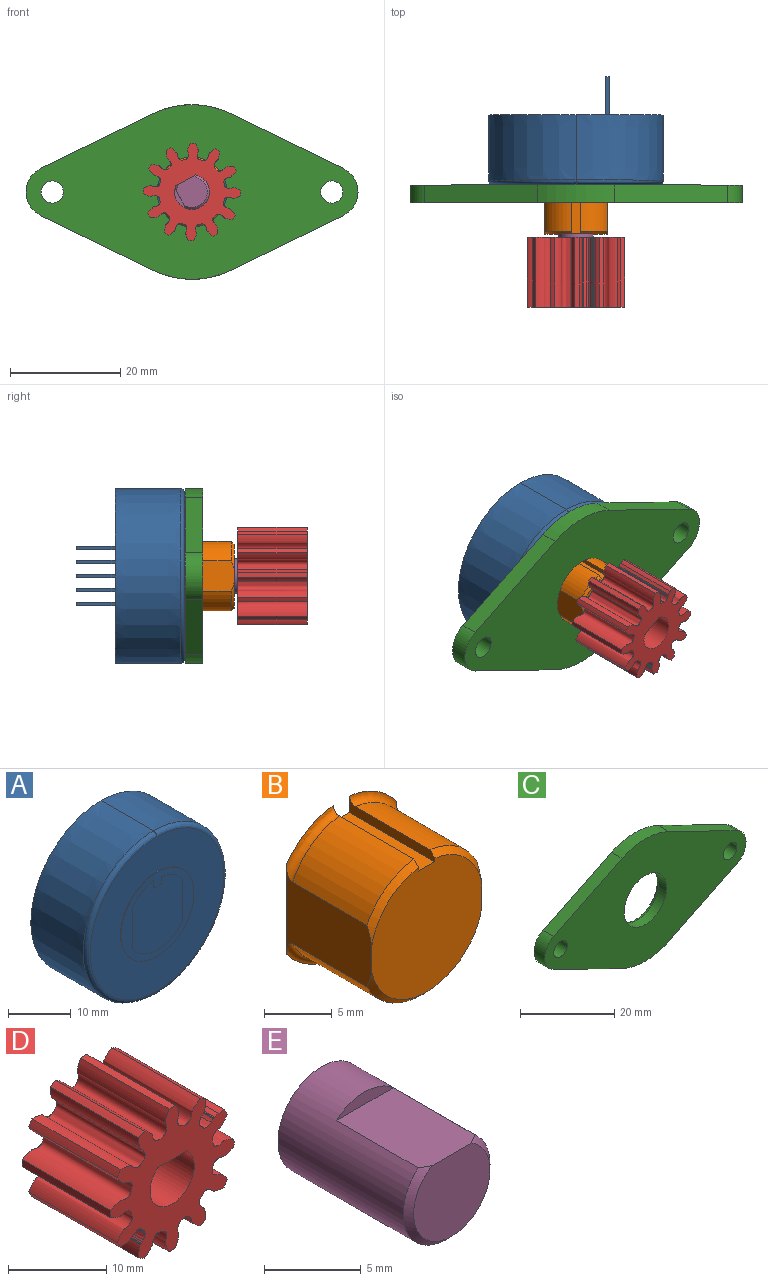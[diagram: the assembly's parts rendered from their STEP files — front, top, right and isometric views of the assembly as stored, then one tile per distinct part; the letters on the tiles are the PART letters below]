
ASSEMBLY  parts=5 mates=4
PART A: 35 faces, bbox 31.8x19.7x31.8 mm
  f0: plane 30.16x30.16mm, normal (0,-1,0), area 500mm2, adj f29,f30,f32,f33
  f1: plane 31.75x31.75mm, normal (0,1,0), area 789.7mm2, adj f2,f3,f5,f6,f7,f8,f10,f11
  f2: extruded ~31.75x15.88mm, area 589.6mm2, adj f1,f3,f32
  f3: extruded ~31.75x15.88mm, area 589.6mm2, adj f1,f2,f33
  f4: plane 0.64x0.64mm, normal (0,1,0), area 0.4mm2, adj f5,f6,f7,f8
  f5: plane 6.99x0.64mm, normal (0,0,-1), area 4.4mm2, adj f1,f4,f6,f8
  f6: plane 6.99x0.64mm, normal (1,0,0), area 4.4mm2, adj f1,f4,f5,f7
  f7: plane 6.99x0.64mm, normal (0,0,1), area 4.4mm2, adj f1,f4,f6,f8
  f8: plane 6.99x0.64mm, normal (-1,0,0), area 4.4mm2, adj f1,f4,f5,f7
  f9: plane 0.64x0.64mm, normal (0,1,0), area 0.4mm2, adj f10,f11,f12,f13
  f10: plane 6.99x0.64mm, normal (0,0,-1), area 4.4mm2, adj f1,f9,f11,f12
  f11: plane 6.99x0.64mm, normal (1,0,0), area 4.4mm2, adj f1,f9,f10,f13
  f12: plane 6.99x0.64mm, normal (-1,0,0), area 4.4mm2, adj f1,f9,f10,f13
  f13: plane 6.99x0.64mm, normal (0,0,1), area 4.4mm2, adj f1,f9,f11,f12
  f14: plane 0.64x0.64mm, normal (0,1,0), area 0.4mm2, adj f15,f16,f17,f18
  f15: plane 6.99x0.64mm, normal (-1,0,0), area 4.4mm2, adj f1,f14,f16,f17
  f16: plane 6.99x0.64mm, normal (0,0,1), area 4.4mm2, adj f1,f14,f15,f18
  f17: plane 6.99x0.64mm, normal (0,0,-1), area 4.4mm2, adj f1,f14,f15,f18
  f18: plane 6.99x0.64mm, normal (1,0,0), area 4.4mm2, adj f1,f14,f16,f17
  f19: plane 0.64x0.64mm, normal (0,1,0), area 0.4mm2, adj f20,f21,f22,f23
  f20: plane 6.99x0.64mm, normal (0,0,-1), area 4.4mm2, adj f1,f19,f21,f23
  f21: plane 6.99x0.64mm, normal (1,0,0), area 4.4mm2, adj f1,f19,f20,f22
  f22: plane 6.99x0.64mm, normal (0,0,1), area 4.4mm2, adj f1,f19,f21,f23
  f23: plane 6.99x0.64mm, normal (-1,0,0), area 4.4mm2, adj f1,f19,f20,f22
  f24: plane 0.64x0.64mm, normal (0,1,0), area 0.4mm2, adj f25,f26,f27,f28
  f25: plane 6.99x0.64mm, normal (0,0,-1), area 4.4mm2, adj f1,f24,f26,f28
  f26: plane 6.99x0.64mm, normal (1,0,0), area 4.4mm2, adj f1,f24,f25,f27
  f27: plane 6.99x0.64mm, normal (0,0,1), area 4.4mm2, adj f1,f24,f26,f28
  f28: plane 6.99x0.64mm, normal (-1,0,0), area 4.4mm2, adj f1,f24,f25,f27
  f29: extruded ~16.51x8.26mm, area 2.6mm2, adj f0,f30,f31
  f30: extruded ~16.51x8.26mm, area 2.6mm2, adj f0,f29,f31
  f31: plane 16.51x16.51mm, normal (0,-1,0), area 77.2mm2, adj f29,f30,f34
  f32: bspline ~31.75x25.88mm, area 61.3mm2, adj f0,f2,f33
  f33: bspline ~31.75x25.88mm, area 61.3mm2, adj f0,f3,f32
  f34: plane 13.92x11.43mm, normal (0,-1,0), area 136.9mm2, adj f31
PART B: 16 faces, bbox 14.5x8.9x16.1 mm
  f0: cone r=5.84mm half-angle=45deg, axis (0,1,0), area 10.7mm2, adj f3,f5,f13,f14
  f1: cone r=5.84mm half-angle=45deg, axis (0,1,0), area 4.7mm2, adj f3,f6,f12,f13
  f2: cone r=5.84mm half-angle=45deg, axis (0,1,0), area 4.7mm2, adj f3,f4,f10,f14
  f3: plane 11.62x11.43mm, normal (0,-1,0), area 106.2mm2, adj f0,f1,f2,f10,f11,f12,f13,f14
  f4: cylinder r=6.35mm len=7.75mm, axis (0,1,0), area 48.6mm2, adj f2,f9,f10,f14
  f5: cylinder r=6.35mm len=11.43mm, axis (0,1,0), area 110.2mm2, adj f0,f7,f13,f14
  f6: cylinder r=6.35mm len=7.75mm, axis (0,1,0), area 48.6mm2, adj f1,f8,f12,f13
  f7: torus R=6.99mm, axis (0,1,0), area 13.8mm2, adj f5,f13,f14,f15
  f8: torus R=6.99mm, axis (0,1,0), area 6.1mm2, adj f6,f12,f13,f15
  f9: torus R=6.99mm, axis (0,1,0), area 6.1mm2, adj f4,f10,f14,f15
  f10: plane 8.92x1.5mm, normal (-1,0,0), area 7.4mm2, adj f2,f3,f4,f9,f11,f15
  f11: plane 8.89x1.68mm, normal (0,0,1), area 14.9mm2, adj f3,f10,f12,f15
  f12: plane 8.92x1.5mm, normal (1,0,0), area 7.4mm2, adj f1,f3,f6,f8,f11,f15
  f13: plane 8.89x8.03mm, normal (-1,0,0), area 48.9mm2, adj f0,f1,f3,f5,f6,f7,f8,f15
  f14: plane 8.89x8.03mm, normal (1,0,0), area 48.9mm2, adj f0,f2,f3,f4,f5,f7,f9,f15
  f15: plane 13.92x11.43mm, normal (0,1,0), area 136.9mm2, adj f7,f8,f9,f10,f11,f12,f13,f14
PART C: 14 faces, bbox 60.3x3.2x31.8 mm
  f0: plane 20.54x9.99mm, normal (-0.44,0,-0.9), area 72.5mm2, adj f1,f7,f11,f12
  f1: cylinder r=15.88mm len=13.89mm, axis (0,1,0), area 45.6mm2, adj f0,f2,f11,f12
  f2: plane 20.54x9.99mm, normal (0.44,0,-0.9), area 72.5mm2, adj f1,f3,f11,f12
  f3: cylinder r=4.76mm len=8.57mm, axis (0,1,0), area 33.8mm2, adj f2,f4,f11,f12
  f4: plane 20.54x9.99mm, normal (0.44,0,0.9), area 72.5mm2, adj f3,f5,f11,f12
  f5: cylinder r=15.88mm len=13.89mm, axis (0,1,0), area 45.6mm2, adj f4,f6,f11,f12
  f6: plane 20.54x9.99mm, normal (-0.44,0,0.9), area 72.5mm2, adj f5,f7,f11,f12
  f7: cylinder r=4.76mm len=8.57mm, axis (0,1,0), area 33.8mm2, adj f0,f6,f11,f12
  f8: cylinder r=2.02mm len=4.04mm, axis (0,1,0), area 40.3mm2, adj f11,f12
  f9: cylinder r=2.02mm len=4.04mm, axis (0,1,0), area 40.3mm2, adj f11,f12
  f10: cylinder r=6.35mm len=12.7mm, axis (0,1,0), area 95mm2, adj f11,f13
  f11: plane 60.33x31.75mm, normal (0,-1,0), area 1069.4mm2, adj f0,f1,f2,f3,f4,f5,f6,f7
  f12: plane 60.33x31.75mm, normal (0,1,0), area 1035.7mm2, adj f0,f1,f2,f3,f4,f5,f6,f7
  f13: torus R=7.14mm, axis (0,-1,0), area 52mm2, adj f10,f12
PART D: 68 faces, bbox 18x19.2x18 mm
  f0: plane 17.95x17.95mm, normal (0,-1,0), area 143.8mm2, adj f1,f2,f3,f4,f5,f6,f7,f8
  f1: bspline ~19x1.59mm, area 19.4mm2, adj f0,f42,f53,f64
  f2: bspline ~19x0.24mm, area 1mm2, adj f0,f54,f55,f64
  f3: bspline ~19x0.35mm, area 2.9mm2, adj f0,f55,f56,f64
  f4: bspline ~19x0.28mm, area 0.9mm2, adj f0,f56,f57,f64
  f5: bspline ~19x0.24mm, area 0.6mm2, adj f0,f57,f58,f64
  f6: bspline ~19x0.2mm, area 0.4mm2, adj f0,f58,f59,f64
  f7: bspline ~19x0.5mm, area 3.2mm2, adj f0,f59,f60,f64
  f8: bspline ~19x0.49mm, area 5.4mm2, adj f0,f60,f61,f64
  f9: bspline ~19x0.28mm, area 1.3mm2, adj f0,f61,f62,f64
  f10: bspline ~19x0.95mm, area 10.1mm2, adj f0,f41,f62,f64
  f11: bspline ~19x1.59mm, area 19.4mm2, adj f0,f35,f44,f64
  f12: bspline ~19x0.24mm, area 1mm2, adj f0,f45,f46,f64
  f13: bspline ~19x0.35mm, area 2.9mm2, adj f0,f46,f47,f64
  f14: bspline ~19x0.28mm, area 0.9mm2, adj f0,f47,f48,f64
  f15: bspline ~19x0.24mm, area 0.6mm2, adj f0,f48,f49,f64
  f16: bspline ~19x0.2mm, area 0.4mm2, adj f0,f49,f50,f64
  f17: bspline ~19x0.5mm, area 3.2mm2, adj f0,f50,f51,f64
  f18: bspline ~19x0.49mm, area 5.4mm2, adj f0,f51,f52,f64
  f19: bspline ~19x0.28mm, area 1.3mm2, adj f0,f52,f63,f64
  f20: bspline ~19x0.95mm, area 10.1mm2, adj f0,f36,f63,f64
  f21: bspline ~19x3.59mm, area 91.1mm2, adj f0,f40,f42,f64
  f22: bspline ~19x3.59mm, area 91.1mm2, adj f0,f39,f40,f64
  f23: bspline ~19x3.56mm, area 91.1mm2, adj f0,f38,f39,f64
  f24: bspline ~19x3.59mm, area 91.1mm2, adj f0,f37,f38,f64
  f25: bspline ~19x3.59mm, area 91.1mm2, adj f0,f36,f37,f64
  f26: bspline ~19x3.59mm, area 91.1mm2, adj f0,f34,f35,f64
  f27: bspline ~19x3.59mm, area 91.1mm2, adj f0,f33,f34,f64
  f28: bspline ~19x3.56mm, area 91.1mm2, adj f0,f32,f33,f64
  f29: bspline ~19x3.59mm, area 91.1mm2, adj f0,f32,f43,f64
  f30: bspline ~19x3.59mm, area 91.1mm2, adj f0,f41,f43,f64
  f31: cylinder r=3.17mm len=12.7mm, axis (0,-1,0), area 195.3mm2, adj f0,f64,f67
  f32: cylinder r=8.89mm len=12.7mm, axis (0,-1,0), area 11.5mm2, adj f0,f28,f29,f64
  f33: cylinder r=8.89mm len=12.7mm, axis (0,-1,0), area 11.5mm2, adj f0,f27,f28,f64
  f34: cylinder r=8.89mm len=12.7mm, axis (0,-1,0), area 11.5mm2, adj f0,f26,f27,f64
  f35: cylinder r=8.89mm len=12.7mm, axis (0,-1,0), area 11.5mm2, adj f0,f11,f26,f64
  f36: cylinder r=8.89mm len=12.7mm, axis (0,-1,0), area 11.5mm2, adj f0,f20,f25,f64
  f37: cylinder r=8.89mm len=12.7mm, axis (0,-1,0), area 11.5mm2, adj f0,f24,f25,f64
  f38: cylinder r=8.89mm len=12.7mm, axis (0,-1,0), area 11.5mm2, adj f0,f23,f24,f64
  f39: cylinder r=8.89mm len=12.7mm, axis (0,-1,0), area 11.5mm2, adj f0,f22,f23,f64
  f40: cylinder r=8.89mm len=12.7mm, axis (0,-1,0), area 11.5mm2, adj f0,f21,f22,f64
  f41: cylinder r=8.89mm len=12.7mm, axis (0,-1,0), area 11.5mm2, adj f0,f10,f30,f64
  f42: cylinder r=8.89mm len=12.7mm, axis (0,-1,0), area 11.5mm2, adj f0,f1,f21,f64
  f43: cylinder r=8.89mm len=12.7mm, axis (0,-1,0), area 11.5mm2, adj f0,f29,f30,f64
  f44: extruded ~12.7x0.04mm, area 0.6mm2, adj f0,f11,f64,f66
  f45: extruded ~12.7x0.05mm, area 0.8mm2, adj f0,f12,f64,f66
  f46: extruded ~12.7x0.11mm, area 1.9mm2, adj f0,f12,f13,f64
  f47: extruded ~12.7x0.61mm, area 8.6mm2, adj f0,f13,f14,f64
  f48: extruded ~12.7x0.15mm, area 2mm2, adj f0,f14,f15,f64
  f49: extruded ~12.7x0.16mm, area 2.3mm2, adj f0,f15,f16,f64
  f50: extruded ~12.7x0.45mm, area 8.1mm2, adj f0,f16,f17,f64
  f51: extruded ~12.7x0.89mm, area 12.3mm2, adj f0,f17,f18,f64
  f52: extruded ~12.7x0.09mm, area 1.5mm2, adj f0,f18,f19,f64
  f53: extruded ~12.7x0.04mm, area 0.6mm2, adj f0,f1,f64,f65
  f54: extruded ~12.7x0.05mm, area 0.8mm2, adj f0,f2,f64,f65
  f55: extruded ~12.7x0.11mm, area 1.9mm2, adj f0,f2,f3,f64
  f56: extruded ~12.7x0.61mm, area 8.6mm2, adj f0,f3,f4,f64
  f57: extruded ~12.7x0.15mm, area 2mm2, adj f0,f4,f5,f64
  f58: extruded ~12.7x0.16mm, area 2.3mm2, adj f0,f5,f6,f64
  f59: extruded ~12.7x0.45mm, area 8.1mm2, adj f0,f6,f7,f64
  f60: extruded ~12.7x0.89mm, area 12.3mm2, adj f0,f7,f8,f64
  f61: extruded ~12.7x0.09mm, area 1.5mm2, adj f0,f8,f9,f64
  f62: extruded ~12.7x0.61mm, area 8.1mm2, adj f0,f9,f10,f64
  f63: extruded ~12.7x0.61mm, area 8.1mm2, adj f0,f19,f20,f64
  f64: plane 17.95x17.95mm, normal (0,1,0), area 140.7mm2, adj f1,f2,f3,f4,f5,f6,f7,f8
  f65: bspline ~19x0.27mm, area 0.1mm2, adj f53,f54,f64
  f66: bspline ~19x0.27mm, area 0.1mm2, adj f44,f45,f64
  f67: plane 12.7x4.16mm, normal (0,0,-1), area 52.8mm2, adj f0,f31,f64
PART E: 6 faces, bbox 6.3x9.5x6.3 mm
  f0: cylinder r=3.17mm len=9.14mm, axis (0,1,0), area 155mm2, adj f1,f3,f4,f5
  f1: plane 4.16x0.78mm, normal (0,-1,0), area 2.2mm2, adj f0,f3
  f2: plane 5.58x5.18mm, normal (0,-1,0), area 23.7mm2, adj f3,f5
  f3: plane 6.35x4.16mm, normal (0,0,1), area 26.2mm2, adj f0,f1,f2,f5
  f4: plane 6.34x6.34mm, normal (0,1,0), area 31.6mm2, adj f0
  f5: cone r=3.17mm half-angle=45deg, axis (0,1,0), area 8mm2, adj f0,f2,f3
PLACE A t=(-15.88,-6.17,15.88)mm
PLACE B t=(-15.88,-6.17,15.88)mm
PLACE C t=(-15.88,-6.17,15.88)mm
PLACE D rot(axis=(0,-1,0),28.7deg) t=(0,-9.55,0)mm
PLACE E rot(axis=(0,-1,0),118.7deg) t=(-6.29,-6.17,-21.55)mm
MATE fastened B.f0 <-> A.f34  axis (0,1,0) through (0,3.18,0)mm
MATE fastened C.f1 <-> A.f34  axis (0,-1,0) through (0,3.18,0)mm
MATE fastened D.f31 <-> E.f0  axis (0,-1,0) through (0,-6.35,0)mm
MATE revolute E.f0 <-> A.f31  axis (0,1,0) through (0,-5.71,0)mm
